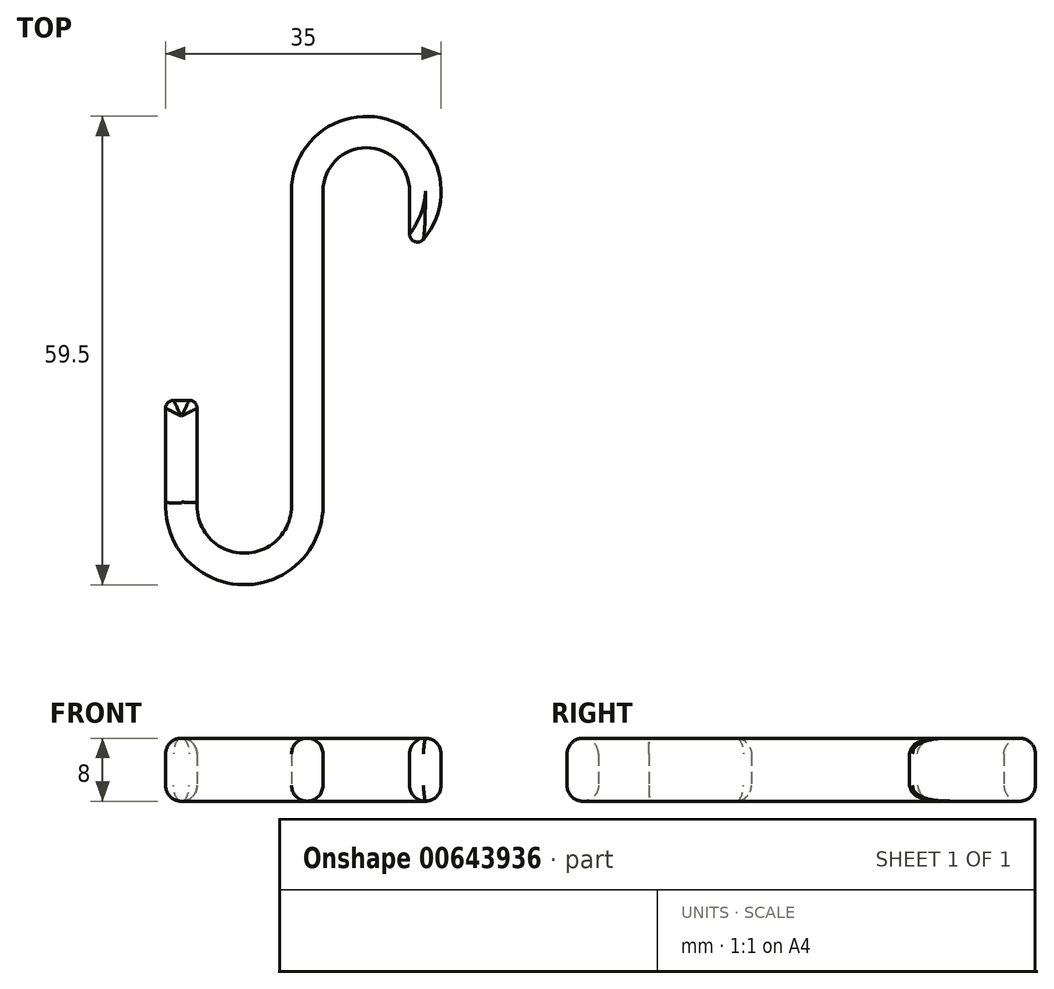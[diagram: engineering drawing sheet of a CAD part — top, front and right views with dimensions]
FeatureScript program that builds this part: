
annotation { "Feature Type Name" : "Feature", "Feature Type Description" : "" }
export const myFeature = defineFeature(function(context is Context, id is Id, definition is map)
    precondition{}
    {
        {
            var Q0;
            Q0=qCreatedBy(makeId("Top.planeOp"),FACE);
            var sketch = newSketch(context, id + "F0", { "sketchPlane" : qUnion([Q0])});
            skArc(sketch, "E0", {"start": v(5.5, 0) * mm, "mid": v(0, 5.5) * mm, "end": v(-5.5, 0) * mm});
            skArc(sketch, "E1", {"start": v(-21.49, -39.58) * mm, "mid": v(-15.71, -46) * mm, "end": v(-9.5, -40) * mm});
            skArc(sketch, "E2.0", {"start": v(5.5, -7.75) * mm, "mid": v(4.36, 8.44) * mm, "end": v(-9.5, 0) * mm});
            skLineSegment(sketch, "E3", {"start": v(-9.5, 0) * mm, "end": v(-9.5, -41.8) * mm, "construction": true});
            skArc(sketch, "E4.0", {"start": v(-25.5, -39.58) * mm, "mid": v(-15.71, -50) * mm, "end": v(-5.5, -40) * mm});
            skLineSegment(sketch, "E5", {"start": v(-5.5, 0) * mm, "end": v(-5.5, -40) * mm});
            skLineSegment(sketch, "E6", {"start": v(-9.5, 0) * mm, "end": v(-9.5, -32) * mm});
            skLineSegment(sketch, "E7", {"start": v(-25.5, -39.58) * mm, "end": v(-25.5, -26.58) * mm});
            skLineSegment(sketch, "E8", {"start": v(-21.49, -39.58) * mm, "end": v(-21.49, -26.58) * mm});
            skLineSegment(sketch, "E9", {"start": v(-21.49, -26.58) * mm, "end": v(-25.5, -26.58) * mm});
            skLineSegment(sketch, "E10", {"start": v(-9.5, -32) * mm, "end": v(-9.5, -40) * mm});
            skLineSegment(sketch, "E11", {"start": v(5.5, 0) * mm, "end": v(5.5, -7.75) * mm});
            skSolve(sketch);
        }
        {
            var Q0;
            Q0 = qSketchRegion(id + "F0", true);
            extrude(context, id + "F1", {"entities" : qUnion([Q0]), "depth" : 8 * mm, "offsetDistance" : 25 * mm});
        }
        {
            var Q0;
            Q0=makeQuery(id+"F1.opExtrude","CAP_FACE",FACE,{"disambiguationData":[OSD([sQuery(id+"F0.wireOp",EDGE,"E0"),sQuery(id+"F0.wireOp",EDGE,"E1"),sQuery(id+"F0.wireOp",EDGE,"E2.0"),sQuery(id+"F0.wireOp",EDGE,"E4.0"),sQuery(id+"F0.wireOp",EDGE,"E5"),sQuery(id+"F0.wireOp",EDGE,"E6"),sQuery(id+"F0.wireOp",EDGE,"E7"),sQuery(id+"F0.wireOp",EDGE,"E8"),sQuery(id+"F0.wireOp",EDGE,"E9"),sQuery(id+"F0.wireOp",EDGE,"E10"),sQuery(id+"F0.wireOp",EDGE,"E11")])],"isStart":false});
            var Q1;
            Q1=makeQuery(id+"F1.opExtrude","CAP_FACE",FACE,{"disambiguationData":[OSD([sQuery(id+"F0.wireOp",EDGE,"E0"),sQuery(id+"F0.wireOp",EDGE,"E1"),sQuery(id+"F0.wireOp",EDGE,"E2.0"),sQuery(id+"F0.wireOp",EDGE,"E4.0"),sQuery(id+"F0.wireOp",EDGE,"E5"),sQuery(id+"F0.wireOp",EDGE,"E6"),sQuery(id+"F0.wireOp",EDGE,"E7"),sQuery(id+"F0.wireOp",EDGE,"E8"),sQuery(id+"F0.wireOp",EDGE,"E9"),sQuery(id+"F0.wireOp",EDGE,"E10"),sQuery(id+"F0.wireOp",EDGE,"E11")])],"isStart":true});
            fillet(context, id + "F2", {"entities" : qUnion([Q0, Q1]), "radius" : 2 * mm, "tangentPropagation" : true, "allowEdgeOverflow" : false});
        }
        {
            var Q0;
            Q0=makeQuery(id+"F1.opExtrude","SWEPT_FACE",FACE,{"disambiguationData":[OSD([sQuery(id+"F0.wireOp",EDGE,"E9")])]});
            fillet(context, id + "F3", {"entities" : qUnion([Q0]), "radius" : 1 * mm, "tangentPropagation" : true, "allowEdgeOverflow" : false});
        }
        {
            var Q0;
            Q0=makeQuery(id+"F1.opExtrude","SWEPT_EDGE",EDGE,{"disambiguationData":[OSD([sQuery(id+"F0.wireOp",EDGE,"E2.0"),sQuery(id+"F0.wireOp",EDGE,"E11")])]});
            var Q1;
            Q1=makeQuery(id+"F2.opFillet","BLEND_EDGE",EDGE,{"blendedFrom":[makeQuery(id+"F1.opExtrude","CAP_EDGE",EDGE,{"disambiguationData":[OSD([sQuery(id+"F0.wireOp",EDGE,"E2.0")])],"isStart":false}),makeQuery(id+"F1.opExtrude","CAP_EDGE",EDGE,{"disambiguationData":[OSD([sQuery(id+"F0.wireOp",EDGE,"E11")])],"isStart":false})],"blendedInto":[]});
            var Q2;
            Q2=makeQuery(id+"F2.opFillet","BLEND_EDGE",EDGE,{"blendedFrom":[makeQuery(id+"F1.opExtrude","CAP_EDGE",EDGE,{"disambiguationData":[OSD([sQuery(id+"F0.wireOp",EDGE,"E2.0")])],"isStart":true}),makeQuery(id+"F1.opExtrude","CAP_EDGE",EDGE,{"disambiguationData":[OSD([sQuery(id+"F0.wireOp",EDGE,"E11")])],"isStart":true})],"blendedInto":[]});
            fillet(context, id + "F4", {"entities" : qUnion([Q0, Q1, Q2]), "radius" : 1 * mm, "tangentPropagation" : true, "allowEdgeOverflow" : false});
        }
    });
